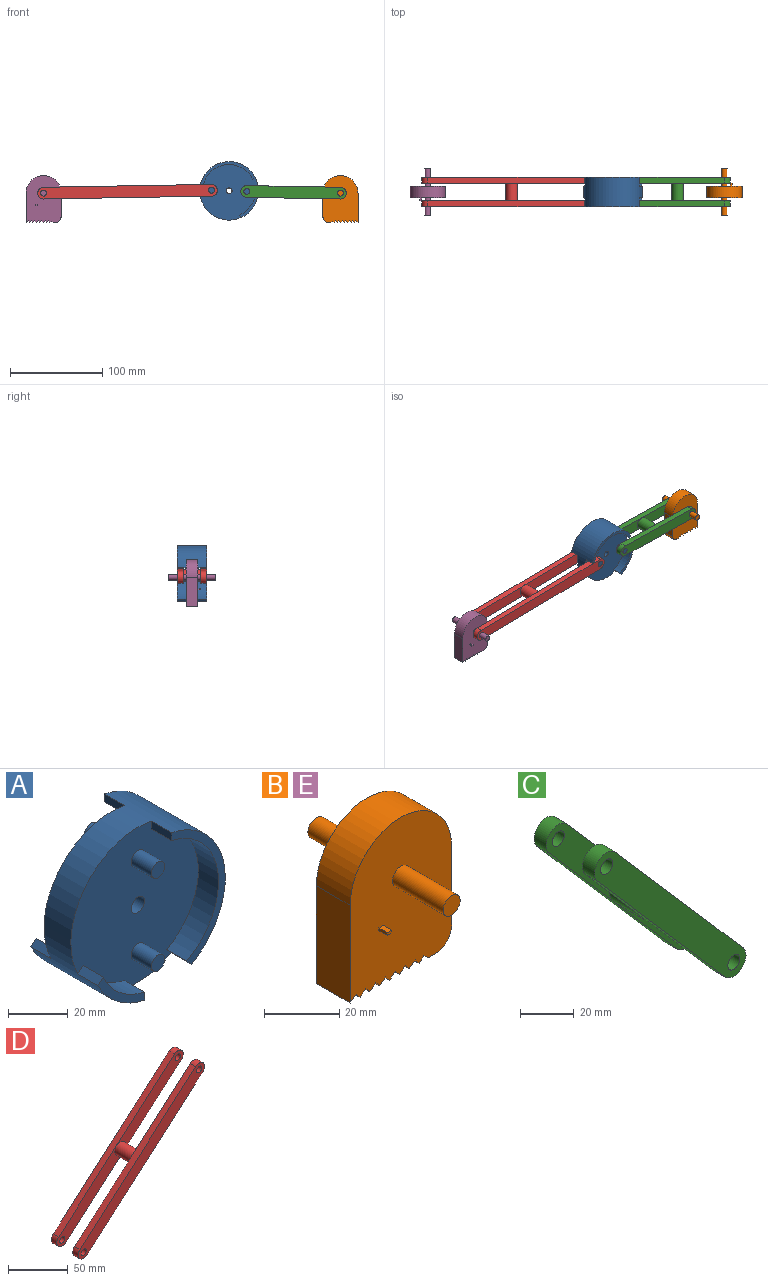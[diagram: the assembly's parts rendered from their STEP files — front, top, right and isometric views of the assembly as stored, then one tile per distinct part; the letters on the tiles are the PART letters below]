
ASSEMBLY  parts=5 mates=9
PART A: 28 faces, bbox 63.5x31.8x63.5 mm
  f0: plane 63.5x60.33mm, normal (0,-1,0), area 2752.8mm2, adj f5,f6,f11,f12,f15,f17,f22,f24
  f1: plane 63.5x60.33mm, normal (0,1,0), area 2752.8mm2, adj f3,f4,f9,f10,f14,f16,f22,f23
  f2: plane 58.65x25.4mm, normal (0,1,0), area 231.7mm2, adj f3,f4,f23,f27
  f3: plane 9.53x3.25mm, normal (-1,0,0), area 30.9mm2, adj f1,f2,f23,f27
  f4: plane 9.53x2.45mm, normal (-0.75,0,-0.66), area 30.9mm2, adj f1,f2,f23,f27
  f5: plane 9.53x2.45mm, normal (-0.75,0,-0.66), area 30.9mm2, adj f0,f7,f24,f27
  f6: plane 9.53x3.25mm, normal (-1,0,0), area 30.9mm2, adj f0,f7,f24,f27
  f7: plane 58.65x25.4mm, normal (0,-1,0), area 231.7mm2, adj f5,f6,f24,f27
  f8: plane 22.1x19.18mm, normal (0,1,0), area 87.4mm2, adj f9,f10,f25,f27
  f9: plane 9.53x3.25mm, normal (1,0,0), area 30.9mm2, adj f1,f8,f25,f27
  f10: plane 9.53x2.49mm, normal (-0.66,0,0.75), area 31.4mm2, adj f1,f8,f25,f27
  f11: plane 9.53x2.49mm, normal (-0.66,0,0.75), area 31.4mm2, adj f0,f13,f26,f27
  f12: plane 9.53x3.25mm, normal (1,0,0), area 30.9mm2, adj f0,f13,f26,f27
  f13: plane 22.1x19.18mm, normal (0,-1,0), area 87.4mm2, adj f11,f12,f26,f27
  f14: cylinder r=3.17mm len=9.53mm, axis (0,1,0), area 190mm2, adj f1,f20
  f15: cylinder r=3.17mm len=9.53mm, axis (0,1,0), area 190mm2, adj f0,f19
  f16: cylinder r=3.17mm len=9.53mm, axis (0,1,0), area 190mm2, adj f1,f21
  f17: cylinder r=3.17mm len=9.53mm, axis (0,1,0), area 190mm2, adj f0,f18
  f18: plane 6.35x6.35mm, normal (0,-1,0), area 31.7mm2, adj f17
  f19: plane 6.35x6.35mm, normal (0,-1,0), area 31.7mm2, adj f15
  f20: plane 6.35x6.35mm, normal (0,1,0), area 31.7mm2, adj f14
  f21: plane 6.35x6.35mm, normal (0,1,0), area 31.7mm2, adj f16
  f22: cylinder r=3.17mm len=12.7mm, axis (0,-1,0), area 253.4mm2, adj f0,f1
  f23: cylinder r=28.57mm len=52.96mm, axis (0,1,0), area 658.4mm2, adj f1,f2,f3,f4
  f24: cylinder r=28.57mm len=52.96mm, axis (0,1,0), area 658.4mm2, adj f0,f5,f6,f7
  f25: cylinder r=28.57mm len=19.62mm, axis (0,1,0), area 249.4mm2, adj f1,f8,f9,f10
  f26: cylinder r=28.57mm len=19.62mm, axis (0,1,0), area 249.4mm2, adj f0,f11,f12,f13
  f27: cylinder r=31.75mm len=63.5mm, axis (0,-1,0), area 4547.2mm2, adj f0,f1,f2,f3,f4,f5,f6,f7
PART B: 32 faces, bbox 38.1x50.8x50.8 mm
  f0: plane 50.8x38.1mm, normal (0,-1,0), area 1711.8mm2, adj f1,f3,f4,f5,f6,f7,f8,f9
  f1: cylinder r=3.17mm len=19.05mm, axis (0,1,0), area 380mm2, adj f0,f2
  f2: plane 6.35x6.35mm, normal (0,-1,0), area 31.7mm2, adj f1
  f3: plane 12.7x2.3mm, normal (0,0,-1), area 29.3mm2, adj f0,f4,f23,f24
  f4: cylinder r=6.35mm len=12.7mm, axis (0,1,0), area 126.7mm2, adj f0,f3,f5,f24
  f5: plane 25.4x12.7mm, normal (1,0,0), area 322.6mm2, adj f0,f4,f6,f24
  f6: cylinder r=19.05mm len=38.1mm, axis (0,1,0), area 760.1mm2, adj f0,f5,f7,f24
  f7: plane 31.75x12.7mm, normal (-1,0,0), area 403.2mm2, adj f0,f6,f8,f24
  f8: plane 12.7x2.23mm, normal (0.63,0,-0.78), area 36.4mm2, adj f0,f7,f9,f24
  f9: plane 12.7x1.81mm, normal (-0.78,0,-0.63), area 29.6mm2, adj f0,f8,f10,f24
  f10: plane 12.7x2.23mm, normal (0.63,0,-0.78), area 36.4mm2, adj f0,f9,f11,f24
  f11: plane 12.7x1.81mm, normal (-0.78,0,-0.63), area 29.6mm2, adj f0,f10,f12,f24
  f12: plane 12.7x2.23mm, normal (0.63,0,-0.78), area 36.4mm2, adj f0,f11,f13,f24
  f13: plane 12.7x1.81mm, normal (-0.78,0,-0.63), area 29.6mm2, adj f0,f12,f14,f24
  f14: plane 12.7x2.23mm, normal (0.63,0,-0.78), area 36.4mm2, adj f0,f13,f15,f24
  f15: plane 12.7x1.81mm, normal (-0.78,0,-0.63), area 29.6mm2, adj f0,f14,f16,f24
  f16: plane 12.7x2.23mm, normal (0.63,0,-0.78), area 36.4mm2, adj f0,f15,f17,f24
  f17: plane 12.7x1.81mm, normal (-0.78,0,-0.63), area 29.6mm2, adj f0,f16,f18,f24
  f18: plane 12.7x2.23mm, normal (0.63,0,-0.78), area 36.4mm2, adj f0,f17,f19,f24
  f19: plane 12.7x1.81mm, normal (-0.78,0,-0.63), area 29.6mm2, adj f0,f18,f20,f24
  f20: plane 12.7x2.23mm, normal (0.63,0,-0.78), area 36.4mm2, adj f0,f19,f21,f24
  f21: plane 12.7x1.81mm, normal (-0.78,0,-0.63), area 29.6mm2, adj f0,f20,f22,f24
  f22: plane 12.7x1.82mm, normal (0.63,0,-0.78), area 29.8mm2, adj f0,f21,f23,f24
  f23: plane 12.7x1.77mm, normal (-0.64,0,-0.77), area 29.3mm2, adj f0,f3,f22,f24
  f24: plane 50.8x38.1mm, normal (0,1,0), area 1713.4mm2, adj f3,f4,f5,f6,f7,f8,f9,f10
  f25: plane 6.35x6.35mm, normal (0,1,0), area 31.7mm2, adj f26
  f26: cylinder r=3.17mm len=19.05mm, axis (0,1,0), area 380mm2, adj f24,f25
  f27: plane 3.18x0.88mm, normal (-1,0,0), area 2.8mm2, adj f0,f28,f30,f31
  f28: plane 3.18x1.76mm, normal (0,0,-1), area 5.6mm2, adj f0,f27,f29,f31
  f29: plane 3.18x0.88mm, normal (1,0,0), area 2.8mm2, adj f0,f28,f30,f31
  f30: plane 3.18x1.76mm, normal (0,0,1), area 5.6mm2, adj f0,f27,f29,f31
  f31: plane 1.76x0.88mm, normal (0,-1,0), area 1.5mm2, adj f27,f28,f29,f30
PART C: 19 faces, bbox 79.3x31.8x89.4 mm
  f0: cylinder r=6.35mm len=19.05mm, axis (0,1,0), area 760.1mm2, adj f1,f9,f10,f18
  f1: plane 48.86x44.46mm, normal (0,1,0), area 613.5mm2, adj f0,f2,f4,f5,f6
  f2: plane 76.69x66.64mm, normal (-0.75,0,-0.66), area 645.2mm2, adj f1,f3,f6,f8,f9
  f3: cylinder r=6.35mm len=11.14mm, axis (0,1,0), area 126.7mm2, adj f2,f4,f8,f9
  f4: plane 76.69x66.64mm, normal (0.75,0,0.66), area 645.2mm2, adj f1,f3,f6,f8,f9
  f5: cylinder r=3.17mm len=6.35mm, axis (0,1,0), area 126.7mm2, adj f1,f8
  f6: cylinder r=6.35mm len=11.14mm, axis (0,1,0), area 126.7mm2, adj f1,f2,f4,f8
  f7: cylinder r=3.17mm len=6.35mm, axis (0,1,0), area 126.7mm2, adj f8,f9
  f8: plane 89.39x79.34mm, normal (0,-1,0), area 1353.7mm2, adj f2,f3,f4,f5,f6,f7
  f9: plane 48.86x44.46mm, normal (0,1,0), area 613.5mm2, adj f0,f2,f3,f4,f7
  f10: plane 48.86x44.46mm, normal (0,-1,0), area 613.5mm2, adj f0,f11,f12,f13,f16
  f11: plane 76.69x66.64mm, normal (-0.75,0,-0.66), area 645.2mm2, adj f10,f12,f15,f17,f18
  f12: cylinder r=6.35mm len=11.14mm, axis (0,-1,0), area 126.7mm2, adj f10,f11,f13,f17
  f13: plane 76.69x66.64mm, normal (0.75,0,0.66), area 645.2mm2, adj f10,f12,f15,f17,f18
  f14: cylinder r=3.17mm len=6.35mm, axis (0,-1,0), area 126.7mm2, adj f17,f18
  f15: cylinder r=6.35mm len=11.14mm, axis (0,-1,0), area 126.7mm2, adj f11,f13,f17,f18
  f16: cylinder r=3.17mm len=6.35mm, axis (0,-1,0), area 126.7mm2, adj f10,f17
  f17: plane 89.39x79.34mm, normal (0,1,0), area 1353.7mm2, adj f11,f12,f13,f14,f15,f16
  f18: plane 48.86x44.46mm, normal (0,-1,0), area 613.5mm2, adj f0,f11,f13,f14,f15
PART D: 19 faces, bbox 150.1x31.8x132.1 mm
  f0: plane 79.24x70.86mm, normal (0,1,0), area 1124.5mm2, adj f1,f3,f4,f5,f9
  f1: plane 137.44x119.43mm, normal (-0.66,0,0.75), area 1156.2mm2, adj f0,f2,f4,f7,f8
  f2: cylinder r=6.35mm len=11.14mm, axis (0,1,0), area 126.7mm2, adj f1,f3,f7,f8
  f3: plane 137.44x119.43mm, normal (0.66,0,-0.75), area 1156.2mm2, adj f0,f2,f4,f7,f8
  f4: cylinder r=6.35mm len=11.14mm, axis (0,1,0), area 126.7mm2, adj f0,f1,f3,f7
  f5: cylinder r=3.17mm len=6.35mm, axis (0,1,0), area 126.7mm2, adj f0,f7
  f6: cylinder r=3.17mm len=6.35mm, axis (0,1,0), area 126.7mm2, adj f7,f8
  f7: plane 150.14x132.13mm, normal (0,-1,0), area 2375.8mm2, adj f1,f2,f3,f4,f5,f6
  f8: plane 79.24x70.86mm, normal (0,1,0), area 1124.5mm2, adj f1,f2,f3,f6,f9
  f9: cylinder r=6.35mm len=19.05mm, axis (0,1,0), area 760.1mm2, adj f0,f8,f10,f18
  f10: plane 79.24x70.86mm, normal (0,-1,0), area 1124.5mm2, adj f9,f11,f12,f13,f16
  f11: plane 137.44x119.43mm, normal (-0.66,0,0.75), area 1156.2mm2, adj f10,f12,f14,f17,f18
  f12: cylinder r=6.35mm len=11.14mm, axis (0,-1,0), area 126.7mm2, adj f10,f11,f13,f17
  f13: plane 137.44x119.43mm, normal (0.66,0,-0.75), area 1156.2mm2, adj f10,f12,f14,f17,f18
  f14: cylinder r=6.35mm len=11.14mm, axis (0,-1,0), area 126.7mm2, adj f11,f13,f17,f18
  f15: cylinder r=3.17mm len=6.35mm, axis (0,-1,0), area 126.7mm2, adj f17,f18
  f16: cylinder r=3.17mm len=6.35mm, axis (0,-1,0), area 126.7mm2, adj f10,f17
  f17: plane 150.14x132.13mm, normal (0,1,0), area 2375.8mm2, adj f11,f12,f13,f14,f15,f16
  f18: plane 79.24x70.86mm, normal (0,-1,0), area 1124.5mm2, adj f9,f11,f13,f14,f15
PART E: same geometry as B
PLACE A rot(axis=(0,-1,0),88deg) t=(63.72,6.23,-98.13)mm
PLACE B rot(axis=(0,0,1),180deg) t=(46.9,6.23,-0.23)mm
PLACE C rot(axis=(0,-1,0),48deg) t=(68.6,6.23,-86.05)mm
PLACE D rot(axis=(0,1,0),40deg) t=(32.43,6.23,-112.06)mm
PLACE E t=(0.07,6.23,-0.23)mm fixed
MATE planar D.f9 <-> A.f16  axis (0,-1,0) through (-46.35,-9.64,-99.04)mm
MATE cylindrical D.f2 <-> E.f1  axis (0,1,0) through (-137.37,-6.47,-100.61)mm
MATE cylindrical C.f3 <-> B.f1  axis (0,-1,0) through (184.34,-9.64,-100.61)mm
MATE cylindrical A.f14 <-> C.f5  axis (0,1,0) through (82.76,-4.88,-98.8)mm
MATE cylindrical A.f16 <-> D.f4  axis (0,1,0) through (44.68,-4.88,-97.47)mm
MATE planar E.f28 <-> B.f28  axis (0,0,-1) through (-144.77,-1.7,-114.22)mm
MATE planar A.f14 <-> C.f0  axis (0,-1,0) through (82.76,-9.64,-98.8)mm
MATE planar E.f1 <-> D.f9  axis (0,-1,0) through (-137.37,-19.17,-100.61)mm
MATE planar B.f1 <-> E.f1  axis (0,-1,0) through (184.34,-19.17,-100.61)mm
